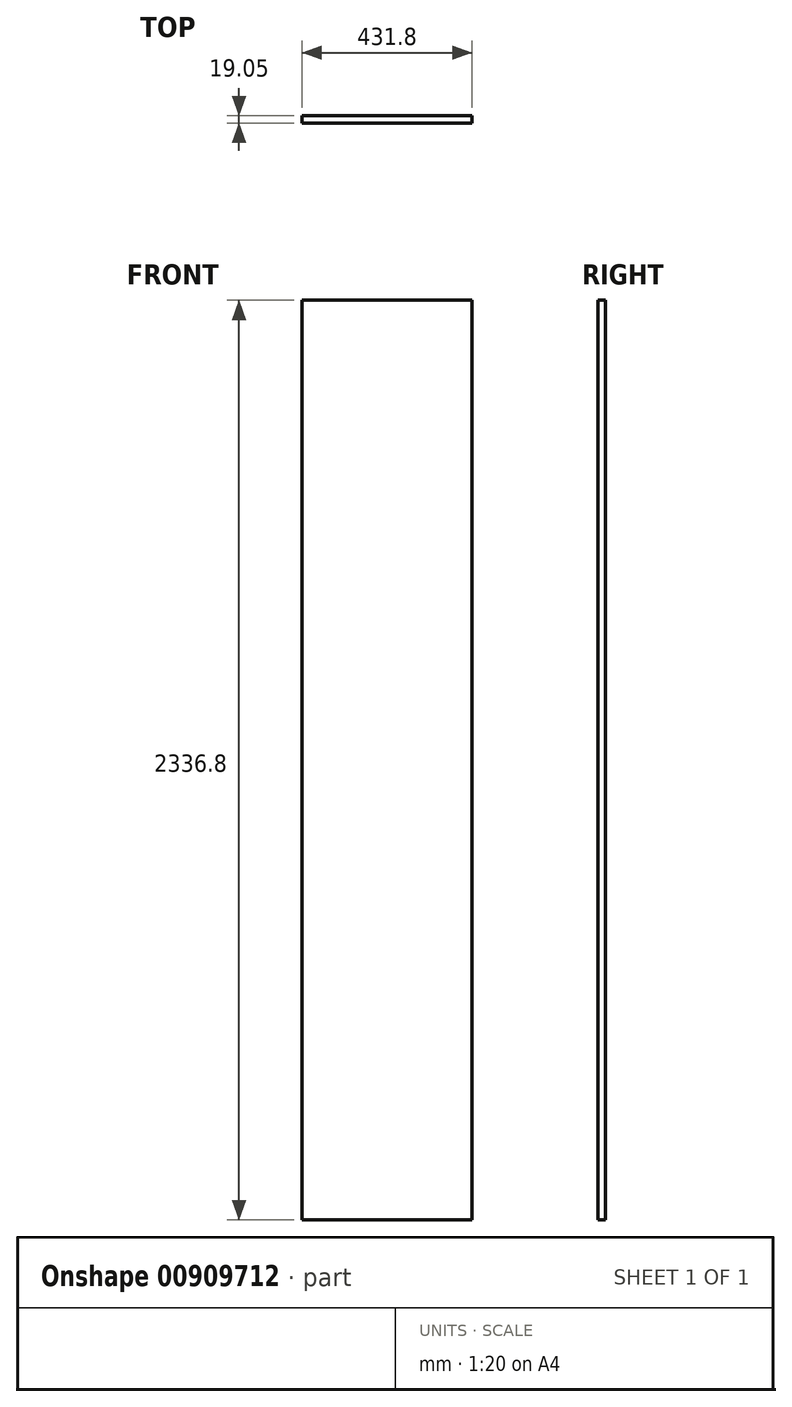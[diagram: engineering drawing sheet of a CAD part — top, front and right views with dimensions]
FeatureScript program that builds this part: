
annotation { "Feature Type Name" : "Feature", "Feature Type Description" : "" }
export const myFeature = defineFeature(function(context is Context, id is Id, definition is map)
    precondition{}
    {
        {
            var Q0;
            Q0=qCreatedBy(makeId("Front.planeOp"),FACE);
            var sketch = newSketch(context, id + "F0", { "sketchPlane" : qUnion([Q0])});
            skLineSegment(sketch, "E0.bottom", {"start": v(215.9, -1168.4) * mm, "end": v(-215.9, -1168.4) * mm});
            skLineSegment(sketch, "E0.top", {"start": v(215.9, 1168.4) * mm, "end": v(-215.9, 1168.4) * mm});
            skLineSegment(sketch, "E0.left", {"start": v(215.9, -1168.4) * mm, "end": v(215.9, 1168.4) * mm});
            skLineSegment(sketch, "E0.right", {"start": v(-215.9, -1168.4) * mm, "end": v(-215.9, 1168.4) * mm});
            skPoint(sketch, "E0.middle", {"position": v(0, 0) * mm});
            skSolve(sketch);
        }
        {
            var Q0;
            Q0=makeQuery(id+"F0.imprint","IMPRINT",FACE,{"disambiguationData":[TD([[makeQuery(id+"F0.imprint","IMPRINT",EDGE,{"derivedFrom":sQuery(id+"F0.wireOp",EDGE,"E0.bottom")}),-1.0]])]});
            extrude(context, id + "F1", {"entities" : qUnion([Q0]), "depth" : 19.05 * mm, "offsetDistance" : 25.4 * mm});
        }
    });
